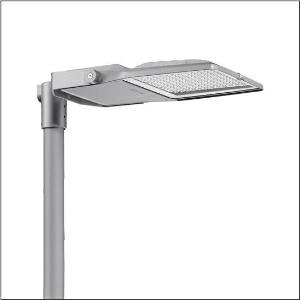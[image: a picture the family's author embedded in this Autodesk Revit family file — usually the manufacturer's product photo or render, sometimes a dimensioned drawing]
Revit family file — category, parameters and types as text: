
# Revit family: floodlight_fl_21_iq_midi___pl33t_5xa7782e2f3a_552b
name_source: partatom
category: Lighting Fixtures
units: mm (PartAtom-declared; Revit-internal decimal feet)

## family parameters
Cut with Voids When Loaded = No
Host = Face
Light Source = No
Part Type = Normal
Room Calculation Point = No
Round Connector Dimension = Use Diameter
Shared = No

## types (1)
- --- (1 x LED, 26540 lm, 208.1 W, 3000K)
    Apparent Load = 208 VA
    CIE Flux Codes = 26 75 99 100 100
    Color Rendering = 70
    Color Temperature = 3000K
    Default Elevation = 1800 mm
    Description = Floodlight FL 21 iQ midi, floodlight, primary light control with lens, of PMMA, primary optical cover: protective disc, of toughened safety glass, transparent, light distribution: PL33T, light emission: direct distribution, installation type: surface-mounted, LED, High Power LED, rated luminous flux: 26.540lm, luminous efficacy: 128lm/W, light colour: 730, colour temperature: 3000K, control gear: ECG iQ, control: optimised constant luminous flux control (CLO 2.0), Desk-Remote (wireless, voltage-free reading and setting of iQ features in the workshop via application-optimized NFC function/RFID function), Smart-Wire, Night-Set, Temp-Guard, Auto-Match, Street-Remote, with terminal, 6-pole, mains connection: 220..240V, AC, 50/60Hz, start of lifetime: 208W, end of service life: 227W, reduction: 90W, luminaire housing, of diecast aluminium, powder-coated, Siteco® metallic grey (DB 702S), corrosivity category C5 mid according to DIN EN ISO 12944, sealing non-destructively replaceable, please order mast flange separately, mast bracket, of steel, galvanised, powder-coated, Siteco® metallic grey (DB 702S), protection rating (complete): IP66, insulation class (complete): insulation class II (safety insulation), certification: CE, protection symbol: D, impact resistance: IK08, permissible operating ambient temperature: -40..+40°C, permissible operating ambient temperature for outdoor applications: -40..+50°C, standard: DIN EN 12944, LABS conformity tested according to VDMA 24364:2018-05, packaging unit: 1 piece

Light Distribution: PL33T
    Height = 76 mm
    Lamp = 1 x LED
    Lamp Light Flux = 26540 lm
    Lamp Power = 208.1 W
    Lamp count = 1
    Length = 657 mm
    Luminous efficacy = 128 lm/W
    Manufacturer = Siteco
    ModVariant = No
    Model = 5XA7782E2F3A
    Number of Poles = 1
    OnlyDefault = Yes
    Power Factor = 1
    Product Name = Floodlight FL 21 iQ midi | PL33T
    Product group = floodlight | pylon annexe
    ProductGroupID = 6200
    Protection Class = Protection class II
    Protection Degree = IP 66
    RLX_Detail_Level = 1
    RLX_Emergency_Light_Flux = 0 lm
    RLX_Emergency_Type = 0
    RLX_Emergency_Type_DB = No
    RlxData = <blob elided: 153733 chars, md5=7c712061>
    Socket = socket
    Standby Power = 0 W
    System Light Flux = 26540 lm
    System Power = 208 W
    Type Comments = factory setting: luminous flux: 100 % | dim-lin: 254 | 710 mA
    Type Image = l_1007123.jpg
    URL = http://relux.com
    VarID = @adj_033957
    Voltage = 0 V
    Weight = 0.00 kg
    Width = 442 mm

## geometry (parser evidence)
native form markers: Blend x4, Sweep x15
no freeform markers — native parametric forms only
